# Revit family: IS_Ceraplus_B8218_BIM_DE
name_source: partatom
category: Plumbing Fixtures
revit_build: Autodesk Revit MEP 2016 (Build: 20161004_0715(x64)
units: mm (PartAtom-declared; Revit-internal decimal feet)

## family parameters
Always vertical = No
Cut with Voids When Loaded = No
OmniClass Number = 23.45.55.17
OmniClass Title = Mixing Faucets
Part Type = Normal
Room Calculation Point = No
Round Connector Dimension = Use Diameter
Shared = No
Work Plane-Based = No

## types (1)
- B8218AA CERAPLUS anti vandal single lever one hole basin mixer with pop-up waste
    Accessories = www.idealstandard.de\ersatzteile
    AreaUnits = millimeters
    AssetType = Fixed
    BIMObjectName = ISI_IdealStandard_
    BIMobject category = Basins
    BOSUseNativeGeometries = 1
    BarCode = 3800861002833
    Brand = Ideal Standard
    Brand url = http://www.idealstandard.co.uk
    CodePerformance = 0
    Color = Chrome
    ConnectionType = Plumbing
    Cost = 0 $
    CurrencyUnit = €
    CurrentRevision = 1
    Date of publishing = 43049
    Description = IS WT-Sicherheitsarm.CERAPLUS,m.Ablgarn, Bedienhebel 120mm, Ausld. 108mm, Chrom
    DurationUnit = year
    EAN code = https://3800861002833
    Edition number = 1
    ExpectedLife = 25
    FaucetFunction = mixed
    FaucetOperation = leverhandle
    FaucetType = pillar
    Features = CERAPLUS anti vandal single lever one hole basin mixer with pop-up waste
    Finish = Chrome
    IFC Classification = Sanitary Terminal
    IfcExportAs = Ifc Valve Type
    Installation instructions = http://www.idealstandard.de
    InstallationInstructions = www.idealstandard.de\produkte
    LinearUnits = millimeters
    MainColor = Chrome
    MaintenanceInformation = www.idealstandard.de\produkte
    Manufacturer name = Ideal Standard
    ManufacturerURL = http://www.idealstandard.com
    Material = Brass
    Material main = Brass
    Model = B8218AA
    ModelNumber = B8218AA
    ModelReference = IS WT-Sicherheitsarm.CERAPLUS,m.Ablgarn, Bedienhebel 120mm, Ausld. 108mm, Chrom
    NBS Reference Code = 35-79-95
    NBS Reference Description = Wash Basin And Trough Water Supply Fittings
    NettWeight = 1,965 kg
    Nominal height = 143
    Nominal width = 114
    NominalDepth = 161 mm
    NominalHeight = 143 mm
    NominalLength = 161 mm
    NominalWidth = 114 mm
    OmniClass Code = 23-31 11 00
    OmniClass Description = Faucets
    Product Guid = 49b90b24-2524-446b-ac52-31d1cdc974d0
    Product SKU = B8218
    Product data url = https://bimobject.com
    Product family = CERAPLUS
    Product group = Basin Mixer
    Product name = CERAPLUS anti vandal single lever one hole basin mixer with pop-up waste
    Product url = http://www.idealstandard.de
    ProductInformation = http://www.idealstandard.de
    QR code = http://bimobject.com
    Shape = Sculptured
    Size = 114x161x143 mm
    Space = Internal
    SpareParts = www.idealstandard.de/ersatzteile
    Technical description = http://www.idealstandard.de
    TestPressure = 10 Bar
    URL = http://www.idealstandard.de
    Uniclass 1.4 Code = L8212
    Uniclass 1.4 Description = Fittings
    Uniclass 2.0 Code = PR-35-79-95
    Uniclass 2.0 Description = Wash Basin And Trough Water Supply Fittings
    Uniclass 2015 Code = Pr_40_20_87_96
    Uniclass 2015 Name = Washbasin manual water supply sets
    Uniclass2015Code = Pr_40_20_87_96
    Uniclass2015Title = Washbasin manual water supply sets
    Uniclass2015Version = Products v1.1
    ValveMechanism = ceramic disc
    ValveOperation = lever
    Version = 1
    VolumeUnits = Litres
    Weight Net (Kg) = 1.97
    WorkingPressure = 1-5 Bar

## geometry (parser evidence)
native form markers: Blend x2, Sweep x3
no freeform markers — native parametric forms only
